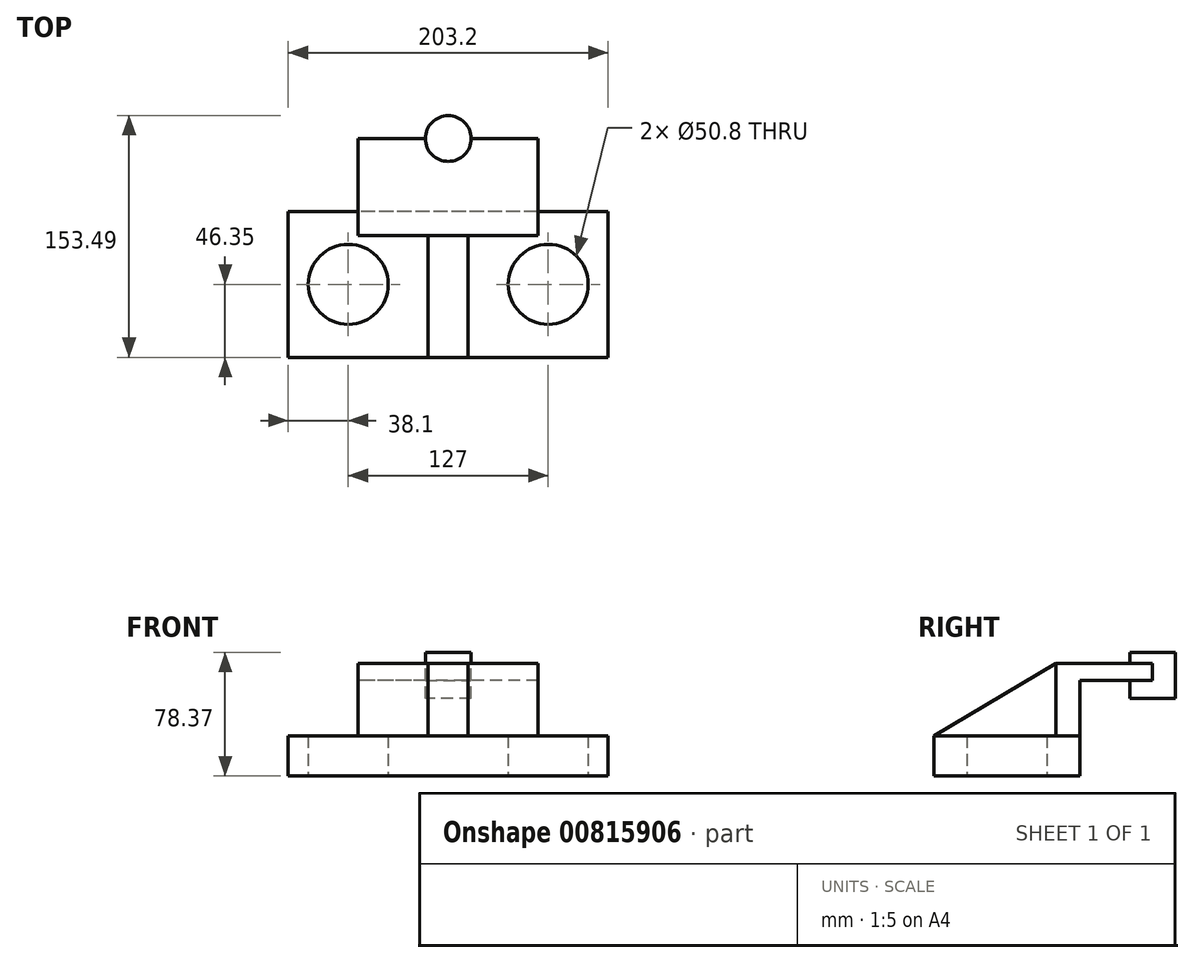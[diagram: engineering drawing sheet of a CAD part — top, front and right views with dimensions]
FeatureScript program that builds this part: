
annotation { "Feature Type Name" : "Feature", "Feature Type Description" : "" }
export const myFeature = defineFeature(function(context is Context, id is Id, definition is map)
    precondition{}
    {
        {
            var Q0;
            Q0=qCreatedBy(makeId("Right.planeOp"),FACE);
            var sketch = newSketch(context, id + "F0", { "sketchPlane" : qUnion([Q0])});
            skLineSegment(sketch, "E0.bottom", {"start": v(-46.35, 12.7) * mm, "end": v(46.35, 12.7) * mm});
            skLineSegment(sketch, "E0.top", {"start": v(-46.35, -12.7) * mm, "end": v(46.35, -12.7) * mm});
            skLineSegment(sketch, "E0.left", {"start": v(-46.35, 12.7) * mm, "end": v(-46.35, -12.7) * mm});
            skLineSegment(sketch, "E0.right", {"start": v(46.35, 12.7) * mm, "end": v(46.35, -12.7) * mm});
            skPoint(sketch, "E0.middle", {"position": v(0, 0) * mm});
            skLineSegment(sketch, "E1.bottom", {"start": v(107.14, 36.58) * mm, "end": v(78.05, 36.58) * mm});
            skLineSegment(sketch, "E1.top", {"start": v(107.14, 65.67) * mm, "end": v(78.05, 65.67) * mm});
            skLineSegment(sketch, "E1.left", {"start": v(107.14, 36.58) * mm, "end": v(107.14, 65.67) * mm});
            skLineSegment(sketch, "E1.right", {"start": v(78.05, 36.58) * mm, "end": v(78.05, 65.67) * mm});
            skPoint(sketch, "E1.middle", {"position": v(92.6, 51.13) * mm});
            skLineSegment(sketch, "E2", {"start": v(46.35, 12.7) * mm, "end": v(46.35, 47.96) * mm});
            skLineSegment(sketch, "E3", {"start": v(46.35, 47.96) * mm, "end": v(92.6, 47.96) * mm});
            skLineSegment(sketch, "E4", {"start": v(31.06, 12.7) * mm, "end": v(31.06, 58.7) * mm});
            skLineSegment(sketch, "E5", {"start": v(31.06, 58.7) * mm, "end": v(92.6, 58.7) * mm});
            skLineSegment(sketch, "E6", {"start": v(92.6, 65.67) * mm, "end": v(92.6, 36.58) * mm});
            skLineSegment(sketch, "E7", {"start": v(-46.35, 12.7) * mm, "end": v(31.06, 58.7) * mm});
            skPoint(sketch, "E8.left.end.orphan", {"position": v(101.7, 60.24) * mm});
            skPoint(sketch, "E9.orphan", {"position": v(101.7, 42) * mm});
            skPoint(sketch, "E8.right.end.orphan", {"position": v(83.47, 60.24) * mm});
            skPoint(sketch, "E8.bottom.end.orphan", {"position": v(83.47, 42) * mm});
            skSolve(sketch);
        }
        {
            var Q0;
            Q0=makeQuery(id+"F0.imprint","IMPRINT",FACE,{"disambiguationData":[TD([[makeQuery(id+"F0.imprint","IMPRINT",EDGE,{"derivedFrom":sQuery(id+"F0.wireOp",EDGE,"E0.top")}),1.0]])]});
            extrude(context, id + "F1", {"entities" : qUnion([Q0]), "endBound" : BoundingType.SYMMETRIC, "depth" : 203.2 * mm, "offsetDistance" : 25.4 * mm});
        }
        {
            var Q0;
            {var subQ2=sQuery(id+"F0.wireOp",EDGE,"E4");Q0=makeQuery(id+"F0.imprint","IMPRINT",FACE,{"disambiguationData":[TD([[makeQuery(id+"F0.imprint","IMPRINT",EDGE,{"derivedFrom":subQ2}),1.0]])]});}
            extrude(context, id + "F2", {"entities" : qUnion([Q0]), "operationType" : NewBodyOperationType.ADD, "endBound" : BoundingType.SYMMETRIC, "depth" : 25.4 * mm, "offsetDistance" : 25.4 * mm});
        }
        {
            var Q0;
            {var subQ1=sQuery(id+"F0.wireOp",EDGE,"E2");Q0=makeQuery(id+"F0.imprint","IMPRINT",FACE,{"disambiguationData":[TD([[makeQuery(id+"F0.imprint","IMPRINT",EDGE,{"derivedFrom":subQ1}),1.0]])]});}
            extrude(context, id + "F3", {"entities" : qUnion([Q0]), "operationType" : NewBodyOperationType.ADD, "endBound" : BoundingType.SYMMETRIC, "depth" : 114.3 * mm, "offsetDistance" : 25.4 * mm});
        }
        {
            var Q0;
            {var subQ0=sQuery(id+"F0.wireOp",EDGE,"E3");var subQ1=sQuery(id+"F0.wireOp",EDGE,"E1.right");var subQ2=makeQuery(id+"F0.imprint","INTERSECT",VERTEX,{"derivedFrom":[subQ1,subQ0]});Q0=makeQuery(id+"F0.imprint","IMPRINT",FACE,{"disambiguationData":[TD([[makeQuery(id+"F0.imprint","IMPRINT",EDGE,{"disambiguationData":[TD([[subQ2,-1.0]])],"derivedFrom":subQ1}),-1.0]])]});}
            var Q1;
            {var subQ0=sQuery(id+"F0.wireOp",EDGE,"E3");var subQ1=sQuery(id+"F0.wireOp",EDGE,"E8.right");var subQ2=makeQuery(id+"F0.imprint","INTERSECT",VERTEX,{"derivedFrom":[subQ1,subQ0]});Q1=makeQuery(id+"F0.imprint","IMPRINT",FACE,{"disambiguationData":[TD([[makeQuery(id+"F0.imprint","IMPRINT",EDGE,{"disambiguationData":[TD([[subQ2,-1.0]])],"derivedFrom":subQ1}),-1.0]])]});}
            extrude(context, id + "F4", {"entities" : qUnion([Q0, Q1]), "operationType" : NewBodyOperationType.ADD, "endBound" : BoundingType.SYMMETRIC, "depth" : 114.3 * mm, "offsetDistance" : 25.4 * mm});
        }
        {
            var Q0;
            {var subQ4=sQuery(id+"F0.wireOp",EDGE,"E1.left");Q0=makeQuery(id+"F0.imprint","IMPRINT",FACE,{"disambiguationData":[TD([[makeQuery(id+"F0.imprint","IMPRINT",EDGE,{"derivedFrom":subQ4}),1.0]])]});}
            var Q1;
            Q1=sQuery(id+"F0.wireOp",EDGE,"E6");
            revolve(context, id + "F5", {"operationType" : NewBodyOperationType.ADD, "surfaceOperationType" : NewSurfaceOperationType.NEW, "entities" : qUnion([Q0]), "axis" : qUnion([Q1]), "revolveType" : RevolveType.FULL});
        }
        {
            var Q0;
            Q0=qCreatedBy(makeId("Top.planeOp"),FACE);
            var sketch = newSketch(context, id + "F6", { "sketchPlane" : qUnion([Q0])});
            skCircle(sketch, "E10", {"center": v(-63.5, 0) * mm, "radius": 25.4 * mm});
            skCircle(sketch, "E11", {"center": v(63.5, 0) * mm, "radius": 25.4 * mm});
            skSolve(sketch);
        }
        {
            var Q0;
            Q0 = qSketchRegion(id + "F6", true);
            extrude(context, id + "F7", {"entities" : qUnion([Q0]), "operationType" : NewBodyOperationType.REMOVE, "endBound" : BoundingType.SYMMETRIC, "depth" : 25.4 * mm, "offsetDistance" : 25.4 * mm});
        }
    });
